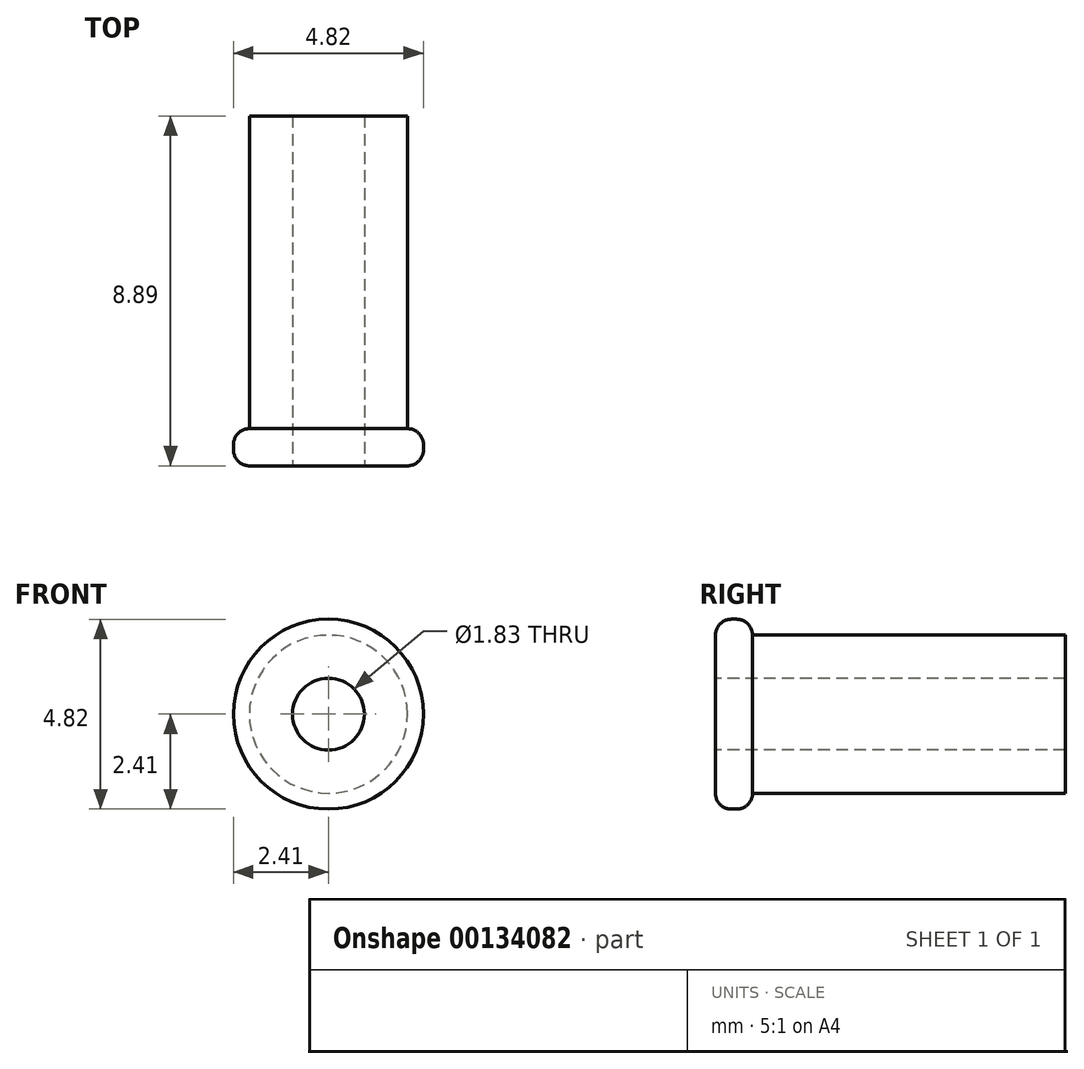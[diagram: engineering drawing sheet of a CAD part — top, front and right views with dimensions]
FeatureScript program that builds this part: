
annotation { "Feature Type Name" : "Feature", "Feature Type Description" : "" }
export const myFeature = defineFeature(function(context is Context, id is Id, definition is map)
    precondition{}
    {
        {
            var Q0;
            Q0=qCreatedBy(makeId("Front.planeOp"),FACE);
            var sketch = newSketch(context, id + "F0", { "sketchPlane" : qUnion([Q0])});
            skCircle(sketch, "E0", {"center": v(0, 0) * mm, "radius": 2 * mm});
            skCircle(sketch, "E1", {"center": v(0, 0) * mm, "radius": 0.91 * mm});
            skCircle(sketch, "E2", {"center": v(0, 0) * mm, "radius": 2.41 * mm});
            skSolve(sketch);
        }
        {
            var Q0;
            Q0=makeQuery(id+"F0.imprint","IMPRINT",FACE,{"disambiguationData":[TD([[makeQuery(id+"F0.imprint","IMPRINT",EDGE,{"derivedFrom":sQuery(id+"F0.wireOp",EDGE,"E0")}),1.0]])]});
            extrude(context, id + "F1", {"entities" : qUnion([Q0]), "oppositeDirection" : true, "depth" : 8.9 * mm});
        }
        {
            var Q0;
            Q0=makeQuery(id+"F0.imprint","IMPRINT",FACE,{"disambiguationData":[TD([[makeQuery(id+"F0.imprint","IMPRINT",EDGE,{"derivedFrom":sQuery(id+"F0.wireOp",EDGE,"E0")}),-1.0]])]});
            extrude(context, id + "F2", {"entities" : qUnion([Q0]), "operationType" : NewBodyOperationType.ADD, "oppositeDirection" : true, "depth" : 0.94 * mm});
        }
        {
            var Q0;
            Q0=makeQuery(id+"F2.opExtrude","CAP_EDGE",EDGE,{"disambiguationData":[OSD([sQuery(id+"F0.wireOp",EDGE,"E2")])],"isStart":false});
            var Q1;
            Q1=makeQuery(id+"F2.opExtrude","CAP_EDGE",EDGE,{"disambiguationData":[OSD([sQuery(id+"F0.wireOp",EDGE,"E2")])],"isStart":true});
            fillet(context, id + "F3", {"entities" : qUnion([Q0, Q1]), "radius" : 0.4 * mm, "tangentPropagation" : true, "allowEdgeOverflow" : false});
        }
    });
